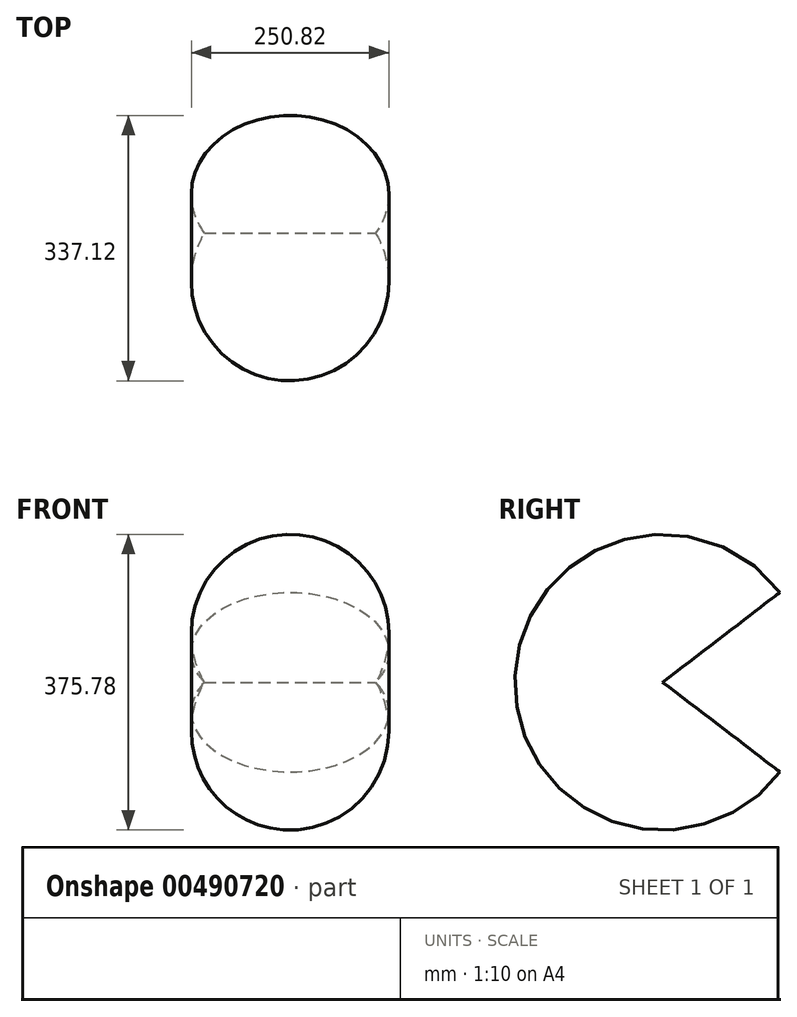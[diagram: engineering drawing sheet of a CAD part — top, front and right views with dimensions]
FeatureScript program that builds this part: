
annotation { "Feature Type Name" : "Feature", "Feature Type Description" : "" }
export const myFeature = defineFeature(function(context is Context, id is Id, definition is map)
    precondition{}
    {
        {
            var Q0;
            Q0=qCreatedBy(makeId("Top.planeOp"),FACE);
            var sketch = newSketch(context, id + "F0", { "sketchPlane" : qUnion([Q0])});
            skLineSegment(sketch, "E0", {"start": v(-108.74, 0) * mm, "end": v(108.74, 0) * mm});
            skArc(sketch, "E1", {"start": v(-108.74, 0) * mm, "mid": v(0, -187.89) * mm, "end": v(108.74, 0) * mm});
            skSolve(sketch);
        }
        {
            var Q0;
            Q0 = qSketchRegion(id + "F0", true);
            var Q1;
            Q1=sQuery(id+"F0.wireOp",EDGE,"E0");
            revolve(context, id + "F1", {"entities" : qUnion([Q0]), "axis" : qUnion([Q1]), "revolveType" : RevolveType.SYMMETRIC, "angle" : 285.17 * degree});
        }
    });
